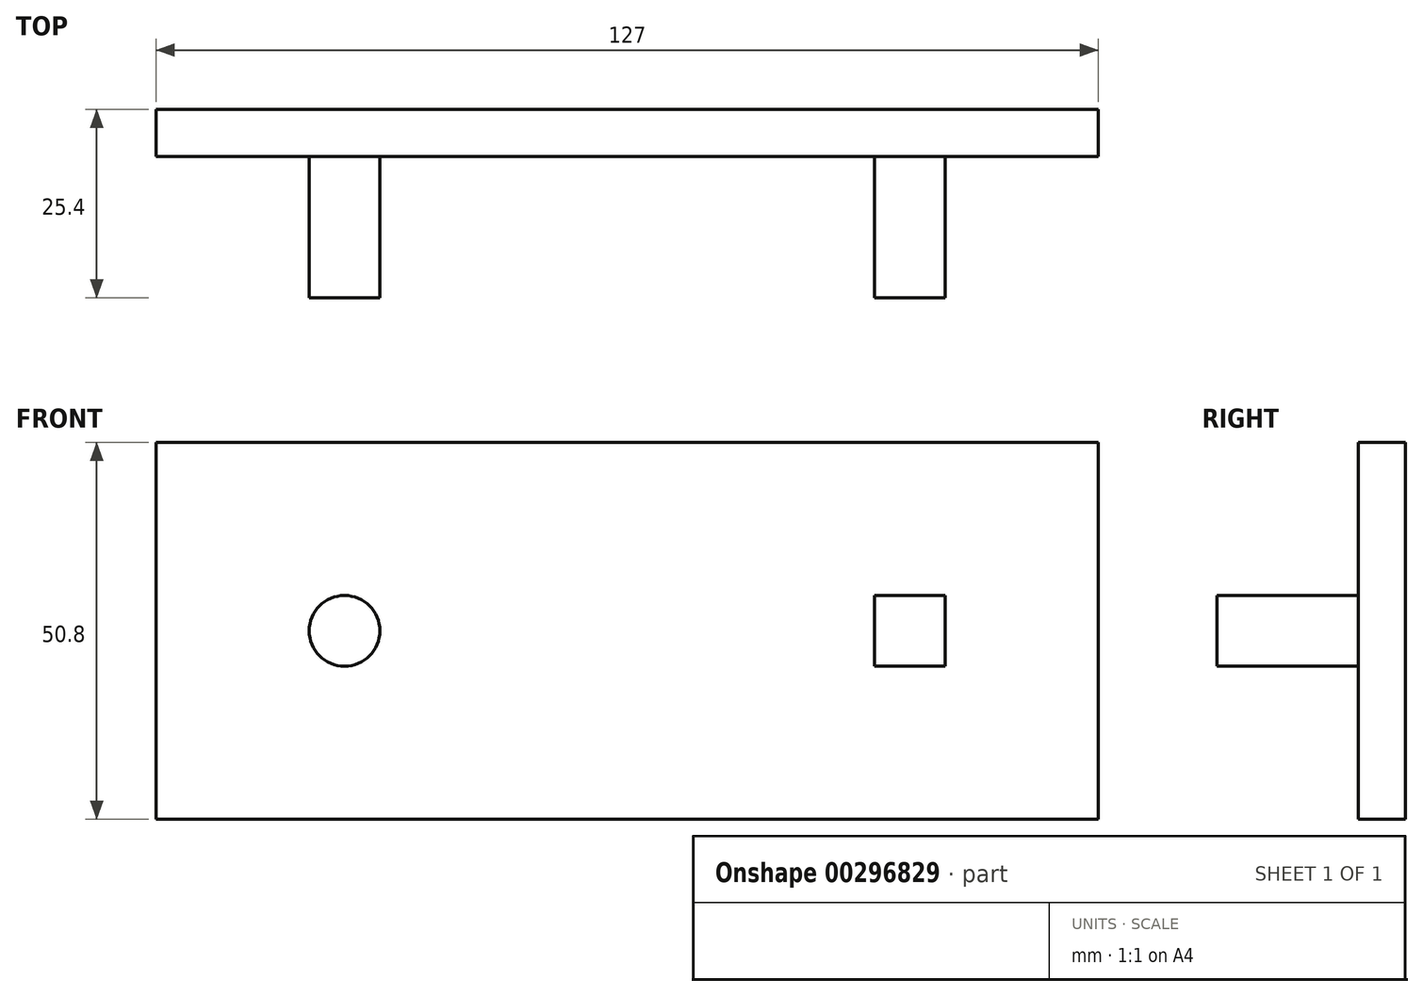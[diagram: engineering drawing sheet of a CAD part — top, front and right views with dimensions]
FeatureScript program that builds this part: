
annotation { "Feature Type Name" : "Feature", "Feature Type Description" : "" }
export const myFeature = defineFeature(function(context is Context, id is Id, definition is map)
    precondition{}
    {
        {
            var Q0;
            Q0=qCreatedBy(makeId("Front.planeOp"),FACE);
            var sketch = newSketch(context, id + "F0", { "sketchPlane" : qUnion([Q0])});
            skLineSegment(sketch, "E0.bottom", {"start": v(0, 0) * mm, "end": v(127, 0) * mm});
            skLineSegment(sketch, "E0.top", {"start": v(0, 50.8) * mm, "end": v(127, 50.8) * mm});
            skLineSegment(sketch, "E0.left", {"start": v(0, 0) * mm, "end": v(0, 50.8) * mm});
            skLineSegment(sketch, "E0.right", {"start": v(127, 0) * mm, "end": v(127, 50.8) * mm});
            skLineSegment(sketch, "E1", {"start": v(0, 0) * mm, "end": v(0, 25.4) * mm});
            skSolve(sketch);
        }
        {
            var Q0;
            Q0=makeQuery(id+"F0.imprint","IMPRINT",FACE,{"disambiguationData":[TD([[makeQuery(id+"F0.imprint","IMPRINT",EDGE,{"derivedFrom":sQuery(id+"F0.wireOp",EDGE,"E0.bottom")}),1.0]])]});
            extrude(context, id + "F1", {"entities" : qUnion([Q0]), "depth" : 6.35 * mm});
        }
        {
            var Q0;
            Q0=makeQuery(id+"F1.opExtrude","CAP_FACE",FACE,{"disambiguationData":[OSD([sQuery(id+"F0.wireOp",EDGE,"E0.bottom"),sQuery(id+"F0.wireOp",EDGE,"E0.top"),sQuery(id+"F0.wireOp",EDGE,"E0.left"),sQuery(id+"F0.wireOp",EDGE,"E0.right"),sQuery(id+"F0.wireOp",EDGE,"E1")])],"isStart":false});
            var sketch = newSketch(context, id + "F2", { "sketchPlane" : qUnion([Q0])});
            skLineSegment(sketch, "E2", {"start": v(0, 0) * mm, "end": v(0, 25.4) * mm});
            skLineSegment(sketch, "E3", {"start": v(0, 25.4) * mm, "end": v(25.4, 25.4) * mm});
            skLineSegment(sketch, "E4", {"start": v(127, 25.4) * mm, "end": v(101.6, 25.4) * mm});
            skCircle(sketch, "E5", {"center": v(25.4, 25.4) * mm, "radius": 4.76 * mm});
            skLineSegment(sketch, "E6.left", {"start": v(101.6, 25.4) * mm, "end": v(101.6, 25.4) * mm});
            skLineSegment(sketch, "E7.bottom", {"start": v(96.84, 30.16) * mm, "end": v(106.36, 30.16) * mm});
            skLineSegment(sketch, "E7.top", {"start": v(96.84, 20.64) * mm, "end": v(106.36, 20.64) * mm});
            skLineSegment(sketch, "E7.left", {"start": v(96.84, 30.16) * mm, "end": v(96.84, 20.64) * mm});
            skLineSegment(sketch, "E7.right", {"start": v(106.36, 30.16) * mm, "end": v(106.36, 20.64) * mm});
            skPoint(sketch, "E7.middle", {"position": v(101.6, 25.4) * mm});
            skSolve(sketch);
        }
        {
            var Q0;
            Q0 = qSketchRegion(id + "F2", true);
            extrude(context, id + "F3", {"entities" : qUnion([Q0]), "operationType" : NewBodyOperationType.ADD, "depth" : 19.05 * mm});
        }
    });
